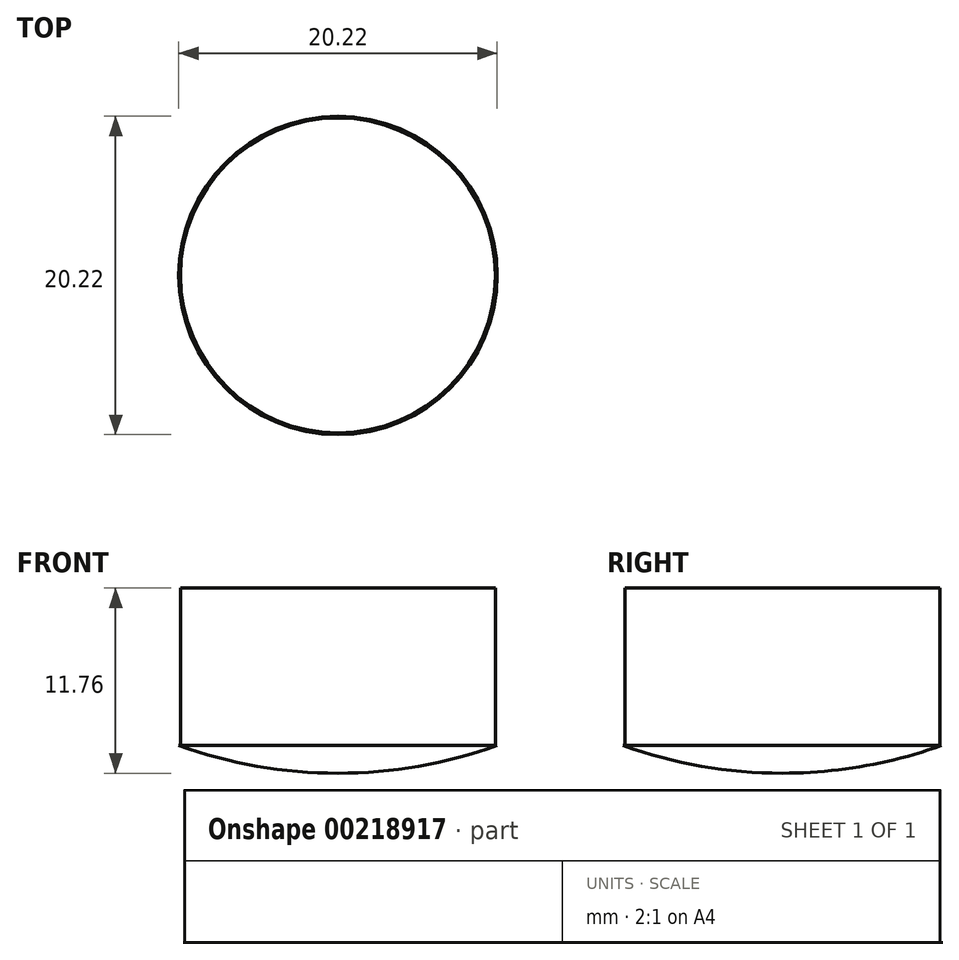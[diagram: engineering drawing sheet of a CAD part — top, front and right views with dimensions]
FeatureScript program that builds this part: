
annotation { "Feature Type Name" : "Feature", "Feature Type Description" : "" }
export const myFeature = defineFeature(function(context is Context, id is Id, definition is map)
    precondition{}
    {
        {
            var Q0;
            Q0=qCreatedBy(makeId("Top.planeOp"),FACE);
            var sketch = newSketch(context, id + "F0", { "sketchPlane" : qUnion([Q0])});
            skCircle(sketch, "E0", {"center": v(0, 0) * mm, "radius": 10 * mm});
            skSolve(sketch);
        }
        {
            var Q0;
            Q0 = qSketchRegion(id + "F0", true);
            extrude(context, id + "F1", {"entities" : qUnion([Q0]), "depth" : 10 * mm, "offsetDistance" : 25 * mm});
        }
        {
            var Q0;
            Q0=qCreatedBy(makeId("Right.planeOp"),FACE);
            var sketch = newSketch(context, id + "F2", { "sketchPlane" : qUnion([Q0])});
            skLineSegment(sketch, "E1", {"start": v(10.11, 0) * mm, "end": v(0, 28.24) * mm, "construction": true});
            skArc(sketch, "E2", {"start": v(10.11, 0) * mm, "mid": v(5.13, -1.31) * mm, "end": v(0, -1.76) * mm});
            skLineSegment(sketch, "E3", {"start": v(0, -1.76) * mm, "end": v(0, 0) * mm});
            skLineSegment(sketch, "E4", {"start": v(0, 0) * mm, "end": v(10.11, 0) * mm});
            skSolve(sketch);
        }
        {
            var Q0;
            Q0 = qSketchRegion(id + "F2", true);
            var Q1;
            Q1=sQuery(id+"F2.wireOp",EDGE,"E3");
            revolve(context, id + "F3", {"operationType" : NewBodyOperationType.ADD, "surfaceOperationType" : NewSurfaceOperationType.NEW, "entities" : qUnion([Q0]), "axis" : qUnion([Q1]), "revolveType" : RevolveType.FULL});
        }
    });
